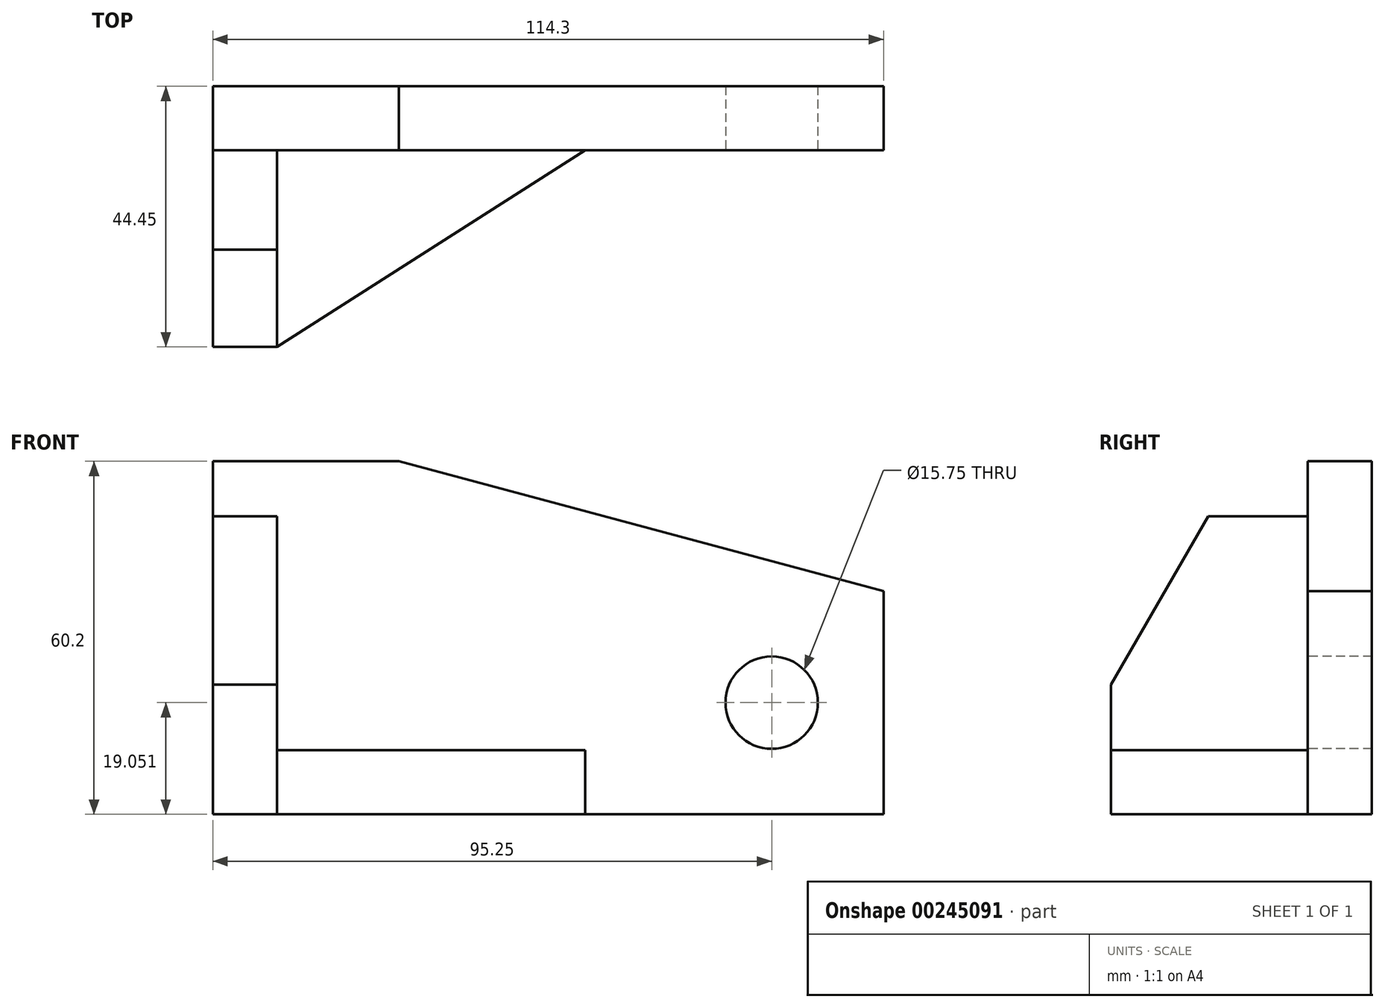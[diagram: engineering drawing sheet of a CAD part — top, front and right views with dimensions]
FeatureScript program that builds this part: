
annotation { "Feature Type Name" : "Feature", "Feature Type Description" : "" }
export const myFeature = defineFeature(function(context is Context, id is Id, definition is map)
    precondition{}
    {
        {
            var Q0;
            Q0=qCreatedBy(makeId("Front.planeOp"),FACE);
            var sketch = newSketch(context, id + "F0", { "sketchPlane" : qUnion([Q0])});
            skLineSegment(sketch, "E0.bottom", {"start": v(-57.15, 30.1) * mm, "end": v(-25.4, 30.1) * mm});
            skLineSegment(sketch, "E0.top", {"start": v(-57.15, -30.1) * mm, "end": v(57.15, -30.1) * mm});
            skLineSegment(sketch, "E0.left", {"start": v(-57.15, 30.1) * mm, "end": v(-57.15, -30.1) * mm});
            skLineSegment(sketch, "E0.right", {"start": v(57.15, 7.98) * mm, "end": v(57.15, -30.1) * mm});
            skLineSegment(sketch, "E1", {"start": v(-25.4, 30.1) * mm, "end": v(57.15, 7.98) * mm});
            skSolve(sketch);
        }
        {
            var Q0;
            Q0=makeQuery(id+"F0.imprint","IMPRINT",FACE,{"disambiguationData":[TD([[makeQuery(id+"F0.imprint","IMPRINT",EDGE,{"derivedFrom":sQuery(id+"F0.wireOp",EDGE,"E0.bottom")}),-1.0]])]});
            extrude(context, id + "F1", {"entities" : qUnion([Q0]), "depth" : 10.92 * mm});
        }
        {
            var Q0;
            Q0=makeQuery(id+"F1.opExtrude","CAP_FACE",FACE,{"disambiguationData":[OSD([sQuery(id+"F0.wireOp",EDGE,"E0.bottom"),sQuery(id+"F0.wireOp",EDGE,"E0.top"),sQuery(id+"F0.wireOp",EDGE,"E0.left"),sQuery(id+"F0.wireOp",EDGE,"E0.right"),sQuery(id+"F0.wireOp",EDGE,"E1")])],"isStart":false});
            var sketch = newSketch(context, id + "F2", { "sketchPlane" : qUnion([Q0])});
            skLineSegment(sketch, "E2", {"start": v(-57.15, 20.7) * mm, "end": v(-46.23, 20.7) * mm});
            skLineSegment(sketch, "E3", {"start": v(-46.23, 20.7) * mm, "end": v(-46.23, -30.1) * mm});
            skSolve(sketch);
        }
        {
            var Q0;
            {var subQ0=sQuery(id+"F2.wireOp",EDGE,"E2");Q0=makeQuery(id+"F2.imprint","IMPRINT",FACE,{"disambiguationData":[TD([[makeQuery(id+"F2.imprint","IMPRINT",EDGE,{"derivedFrom":subQ0}),-1.0]])]});}
            extrude(context, id + "F3", {"entities" : qUnion([Q0]), "operationType" : NewBodyOperationType.ADD, "depth" : 33.53 * mm});
        }
        {
            var Q0;
            Q0=makeQuery(id+"F3.opExtrude","SWEPT_FACE",FACE,{"disambiguationData":[OSD([sQuery(id+"F2.wireOp",EDGE,"E3")])]});
            var sketch = newSketch(context, id + "F4", { "sketchPlane" : qUnion([Q0])});
            skLineSegment(sketch, "E4", {"start": v(-27.88, 20.7) * mm, "end": v(-44.45, -8) * mm});
            skSolve(sketch);
        }
        {
            var Q0;
            {var subQ0=sQuery(id+"F4.wireOp",EDGE,"E4");Q0=makeQuery(id+"F4.imprint","IMPRINT",FACE,{"disambiguationData":[TD([[makeQuery(id+"F4.imprint","IMPRINT",EDGE,{"derivedFrom":subQ0}),-1.0]])]});}
            extrude(context, id + "F5", {"entities" : qUnion([Q0]), "operationType" : NewBodyOperationType.REMOVE, "endBound" : BoundingType.THROUGH_ALL, "oppositeDirection" : true, "depth" : 25.4 * mm});
        }
        {
            var Q0;
            Q0=makeQuery(id+"F1.opExtrude","CAP_FACE",FACE,{"disambiguationData":[OSD([sQuery(id+"F0.wireOp",EDGE,"E0.bottom"),sQuery(id+"F0.wireOp",EDGE,"E0.top"),sQuery(id+"F0.wireOp",EDGE,"E0.left"),sQuery(id+"F0.wireOp",EDGE,"E0.right"),sQuery(id+"F0.wireOp",EDGE,"E1")])],"isStart":false});
            var sketch = newSketch(context, id + "F6", { "sketchPlane" : qUnion([Q0])});
            skLineSegment(sketch, "E5", {"start": v(-46.23, -19.18) * mm, "end": v(6.35, -19.18) * mm});
            skLineSegment(sketch, "E6", {"start": v(6.35, -19.18) * mm, "end": v(6.35, -30.1) * mm});
            skSolve(sketch);
        }
        {
            var Q0;
            {var subQ0=sQuery(id+"F6.wireOp",EDGE,"E5");Q0=makeQuery(id+"F6.imprint","IMPRINT",FACE,{"disambiguationData":[TD([[makeQuery(id+"F6.imprint","IMPRINT",EDGE,{"derivedFrom":subQ0}),-1.0]])]});}
            var Q1;
            Q1=makeQuery(id+"F3.opExtrude","CAP_FACE",FACE,{"disambiguationData":[OSD([sQuery(id+"F0.wireOp",EDGE,"E0.top"),sQuery(id+"F0.wireOp",EDGE,"E0.left"),sQuery(id+"F2.wireOp",EDGE,"E2"),sQuery(id+"F2.wireOp",EDGE,"E3")])],"isStart":false});
            extrude(context, id + "F7", {"entities" : qUnion([Q0]), "operationType" : NewBodyOperationType.ADD, "endBound" : BoundingType.UP_TO_SURFACE, "endBoundEntityFace" : qUnion([Q1]), "depth" : 33.53 * mm});
        }
        {
            var Q0;
            Q0=makeQuery(id+"F7.opExtrude","SWEPT_FACE",FACE,{"disambiguationData":[OSD([sQuery(id+"F6.wireOp",EDGE,"E5")])]});
            var sketch = newSketch(context, id + "F8", { "sketchPlane" : qUnion([Q0])});
            skLineSegment(sketch, "E7", {"start": v(-46.23, -44.45) * mm, "end": v(6.35, -10.92) * mm});
            skSolve(sketch);
        }
        {
            var Q0;
            Q0=makeQuery(id+"F8.imprint","IMPRINT",FACE,{"disambiguationData":[TD([[makeQuery(id+"F8.imprint","IMPRINT",EDGE,{"derivedFrom":sQuery(id+"F8.wireOp",EDGE,"E7")}),-1.0]])]});
            extrude(context, id + "F9", {"entities" : qUnion([Q0]), "operationType" : NewBodyOperationType.REMOVE, "endBound" : BoundingType.THROUGH_ALL, "oppositeDirection" : true, "depth" : 25.4 * mm});
        }
        {
            var Q0;
            Q0=makeQuery(id+"F1.opExtrude","CAP_FACE",FACE,{"disambiguationData":[OSD([sQuery(id+"F0.wireOp",EDGE,"E0.bottom"),sQuery(id+"F0.wireOp",EDGE,"E0.top"),sQuery(id+"F0.wireOp",EDGE,"E0.left"),sQuery(id+"F0.wireOp",EDGE,"E0.right"),sQuery(id+"F0.wireOp",EDGE,"E1")])],"isStart":false});
            var sketch = newSketch(context, id + "F10", { "sketchPlane" : qUnion([Q0])});
            skCircle(sketch, "E8", {"center": v(38.1, -11.05) * mm, "radius": 7.87 * mm});
            skSolve(sketch);
        }
        {
            var Q0;
            Q0=makeQuery(id+"F10.imprint","IMPRINT",FACE,{"disambiguationData":[TD([[makeQuery(id+"F10.imprint","IMPRINT",EDGE,{"derivedFrom":sQuery(id+"F10.wireOp",EDGE,"E8")}),1.0]])]});
            extrude(context, id + "F11", {"entities" : qUnion([Q0]), "operationType" : NewBodyOperationType.REMOVE, "endBound" : BoundingType.THROUGH_ALL, "oppositeDirection" : true, "depth" : 25.4 * mm});
        }
    });
